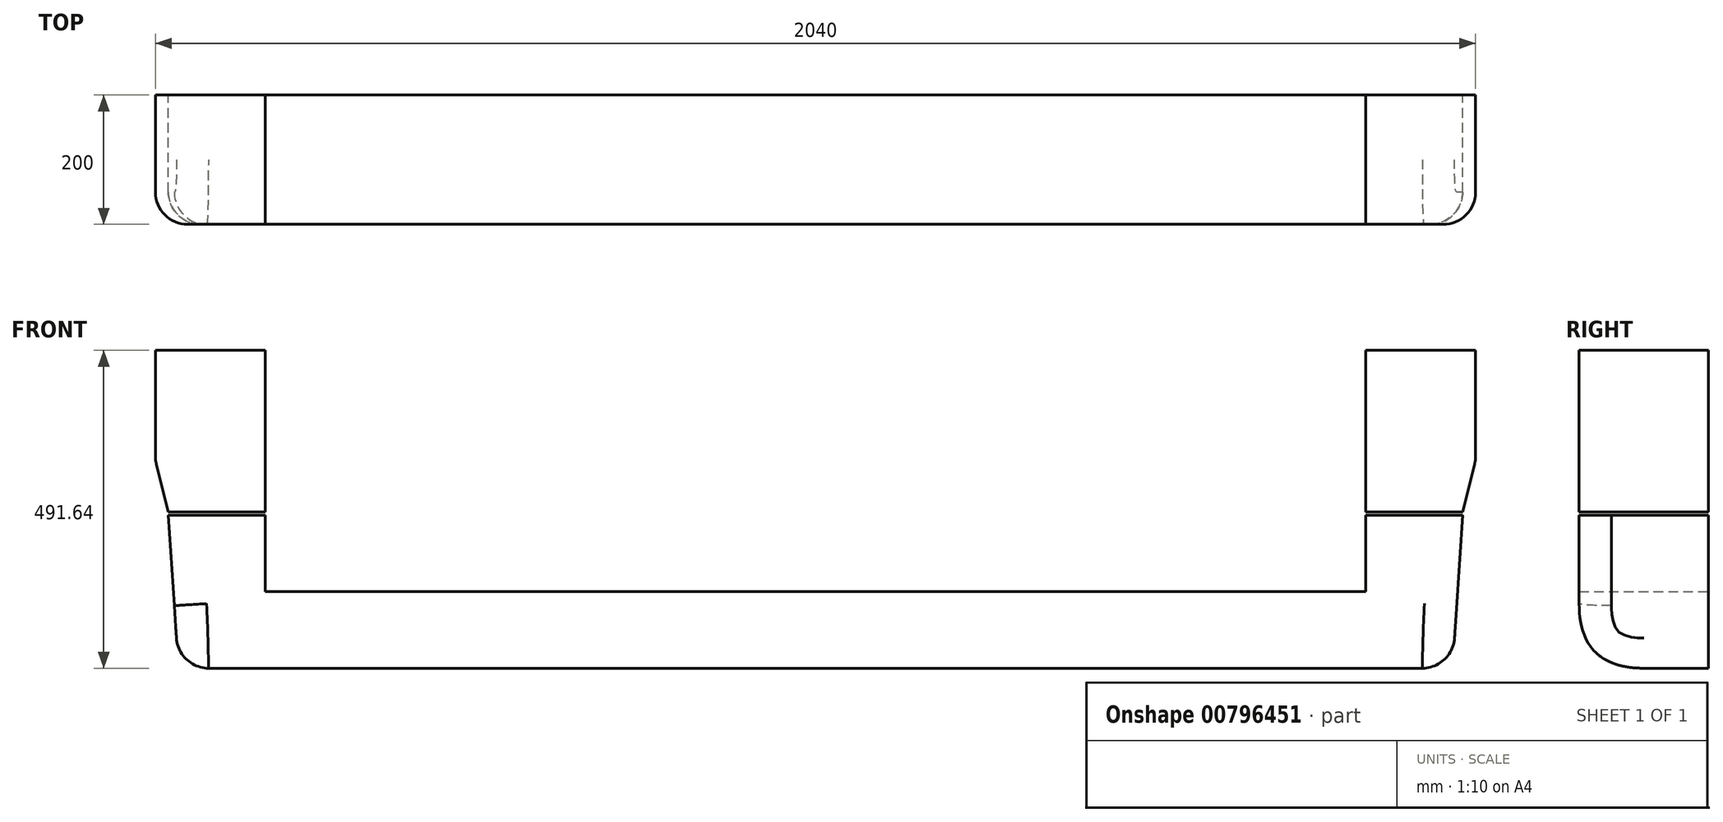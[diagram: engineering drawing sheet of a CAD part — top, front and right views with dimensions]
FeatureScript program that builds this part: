
annotation { "Feature Type Name" : "Feature", "Feature Type Description" : "" }
export const myFeature = defineFeature(function(context is Context, id is Id, definition is map)
    precondition{}
    {
        {
            var Q0;
            Q0=qCreatedBy(makeId("Front.planeOp"),FACE);
            var sketch = newSketch(context, id + "F0", { "sketchPlane" : qUnion([Q0])});
            skLineSegment(sketch, "E0.top", {"start": v(0, -118.32) * mm, "end": v(-950, -118.32) * mm});
            skPoint(sketch, "E0.middle", {"position": v(0, 0) * mm});
            skLineSegment(sketch, "E1.top", {"start": v(-850, 0) * mm, "end": v(0, 0) * mm});
            skLineSegment(sketch, "E1.left", {"start": v(-850, 118.32) * mm, "end": v(-850, 0) * mm});
            skLineSegment(sketch, "E2.trimOffspring", {"start": v(-850, 118.32) * mm, "end": v(-1000, 118.32) * mm});
            skPoint(sketch, "E3.visualSharp", {"position": v(-1000, -118.32) * mm});
            skArc(sketch, "E3.filletArc", {"start": v(-985.36, -103.67) * mm, "mid": v(-969.13, -114.51) * mm, "end": v(-950, -118.32) * mm});
            skPoint(sketch, "E4.visualSharp", {"position": v(1000, -118.32) * mm});
            skLineSegment(sketch, "E5", {"start": v(-1000, 123.32) * mm, "end": v(-850, 123.32) * mm});
            skLineSegment(sketch, "E6", {"start": v(-850, 123.32) * mm, "end": v(-850, 373.32) * mm});
            skLineSegment(sketch, "E7", {"start": v(-850, 373.32) * mm, "end": v(-1000, 373.32) * mm});
            skLineSegment(sketch, "E8", {"start": v(-1000, 118.32) * mm, "end": v(-985.36, -103.67) * mm});
            skLineSegment(sketch, "E9", {"start": v(-1020, 209.43) * mm, "end": v(-1020, 373.32) * mm});
            skLineSegment(sketch, "E10", {"start": v(-1020, 373.32) * mm, "end": v(-1000, 373.32) * mm});
            skLineSegment(sketch, "E11", {"start": v(-1000, 123.32) * mm, "end": v(-1018.5, 197.3) * mm});
            skPoint(sketch, "E12.end.orphan", {"position": v(-1020, 153.28) * mm});
            skPoint(sketch, "E13.visualSharp", {"position": v(-1020, 203.28) * mm});
            skArc(sketch, "E13.filletArc", {"start": v(-1020, 209.43) * mm, "mid": v(-1019.63, 203.32) * mm, "end": v(-1018.5, 197.3) * mm});
            skLineSegment(sketch, "E14", {"start": v(0, 0) * mm, "end": v(0, -118.32) * mm});
            skPoint(sketch, "E1.right.end.orphan", {"position": v(850, 0) * mm});
            skPoint(sketch, "E0.bottom.end.orphan", {"position": v(850, 118.32) * mm});
            skPoint(sketch, "E4.filletArc.start.orphan", {"position": v(950, -118.32) * mm});
            skPoint(sketch, "E15.start.orphan", {"position": v(1000, 118.32) * mm});
            skPoint(sketch, "E16.start.orphan", {"position": v(1000, 123.32) * mm});
            skPoint(sketch, "E17.end.orphan", {"position": v(850, 123.32) * mm});
            skPoint(sketch, "E18.end.orphan", {"position": v(850, 373.32) * mm});
            skLineSegment(sketch, "E19.MirrorCS", {"start": v(850, 0) * mm, "end": v(0, 0) * mm});
            skLineSegment(sketch, "E20.MirrorCS", {"start": v(0, -118.32) * mm, "end": v(950, -118.32) * mm});
            skArc(sketch, "E21.MirrorCS", {"start": v(985.36, -103.67) * mm, "mid": v(969.13, -114.51) * mm, "end": v(950, -118.32) * mm});
            skLineSegment(sketch, "E22.MirrorCS", {"start": v(1000, 118.32) * mm, "end": v(985.36, -103.67) * mm});
            skLineSegment(sketch, "E23.MirrorCS", {"start": v(850, 118.32) * mm, "end": v(850, 0) * mm});
            skLineSegment(sketch, "E24.MirrorCS", {"start": v(850, 123.32) * mm, "end": v(850, 373.32) * mm});
            skLineSegment(sketch, "E25.MirrorCS", {"start": v(1000, 123.32) * mm, "end": v(1018.5, 197.3) * mm});
            skArc(sketch, "E26.MirrorCS", {"start": v(1020, 209.43) * mm, "mid": v(1019.63, 203.32) * mm, "end": v(1018.5, 197.3) * mm});
            skLineSegment(sketch, "E27.MirrorCS", {"start": v(1020, 209.43) * mm, "end": v(1020, 373.32) * mm});
            skLineSegment(sketch, "E28.MirrorCS", {"start": v(1020, 373.32) * mm, "end": v(1000, 373.32) * mm});
            skLineSegment(sketch, "E29.MirrorCS", {"start": v(850, 373.32) * mm, "end": v(1000, 373.32) * mm});
            skLineSegment(sketch, "E30.MirrorCS", {"start": v(1000, 123.32) * mm, "end": v(850, 123.32) * mm});
            skLineSegment(sketch, "E31.MirrorCS", {"start": v(850, 118.32) * mm, "end": v(1000, 118.32) * mm});
            skSolve(sketch);
        }
        {
            var Q0;
            Q0=makeQuery(id+"F0.imprint","IMPRINT",FACE,{"disambiguationData":[TD([[makeQuery(id+"F0.imprint","IMPRINT",EDGE,{"derivedFrom":sQuery(id+"F0.wireOp",EDGE,"E14")}),1.0]])]});
            var Q1;
            Q1=makeQuery(id+"F0.imprint","IMPRINT",FACE,{"disambiguationData":[TD([[makeQuery(id+"F0.imprint","IMPRINT",EDGE,{"derivedFrom":sQuery(id+"F0.wireOp",EDGE,"E0.top")}),-1.0]])]});
            var Q2;
            Q2=makeQuery(id+"F0.imprint","IMPRINT",FACE,{"disambiguationData":[TD([[makeQuery(id+"F0.imprint","IMPRINT",EDGE,{"derivedFrom":sQuery(id+"F0.wireOp",EDGE,"E5")}),1.0]])]});
            var Q3;
            Q3=makeQuery(id+"F0.imprint","IMPRINT",FACE,{"disambiguationData":[TD([[makeQuery(id+"F0.imprint","IMPRINT",EDGE,{"derivedFrom":sQuery(id+"F0.wireOp",EDGE,"E25.MirrorCS")}),1.0]])]});
            extrude(context, id + "F1", {"entities" : qUnion([Q0, Q1, Q2, Q3]), "depth" : 200 * mm, "offsetDistance" : 25.4 * mm});
        }
        {
            var Q0;
            Q0=makeQuery(id+"F1.opExtrude","CAP_EDGE",EDGE,{"disambiguationData":[OSD([sQuery(id+"F0.wireOp",EDGE,"E0.left")])],"isStart":false});
            var Q1;
            Q1=makeQuery(id+"F1.opExtrude","CAP_EDGE",EDGE,{"disambiguationData":[OSD([sQuery(id+"F0.wireOp",EDGE,"E4.filletArc")])],"isStart":false});
            var Q2;
            Q2=makeQuery(id+"F1.opExtrude","CAP_EDGE",EDGE,{"disambiguationData":[OSD([sQuery(id+"F0.wireOp",EDGE,"E0.top")])],"isStart":false});
            var Q3;
            Q3=makeQuery(id+"F1.opExtrude","CAP_EDGE",EDGE,{"disambiguationData":[OSD([sQuery(id+"F0.wireOp",EDGE,"E3.filletArc")])],"isStart":false});
            var Q4;
            Q4=makeQuery(id+"F1.opExtrude","CAP_EDGE",EDGE,{"disambiguationData":[OSD([sQuery(id+"F0.wireOp",EDGE,"E0.right")])],"isStart":false});
            fillet(context, id + "F2", {"entities" : qUnion([Q0, Q1, Q2, Q3, Q4]), "radius" : 100 * mm, "tangentPropagation" : true, "rho" : 0.5, "crossSection" : FilletCrossSection.CONIC, "allowEdgeOverflow" : false});
        }
        {
            var Q0;
            Q0=makeQuery(id+"F2.opFillet","BLEND_EDGE",EDGE,{"blendedFrom":[makeQuery(id+"F1.opExtrude","CAP_EDGE",EDGE,{"disambiguationData":[OSD([sQuery(id+"F0.wireOp",EDGE,"E0.top"),sQuery(id+"F0.wireOp",EDGE,"E20.MirrorCS")])],"isStart":false}),makeQuery(id+"F1.opExtrude","SWEPT_FACE",FACE,{"disambiguationData":[OSD([sQuery(id+"F0.wireOp",EDGE,"E8")])]})],"blendedInto":[makeQuery(id+"F1.opExtrude","SWEPT_FACE",FACE,{"disambiguationData":[OSD([sQuery(id+"F0.wireOp",EDGE,"E8")])]})]});
            var Q1;
            Q1=makeQuery(id+"F1.opExtrude","CAP_EDGE",EDGE,{"disambiguationData":[OSD([sQuery(id+"F0.wireOp",EDGE,"E8")])],"isStart":false});
            var Q2;
            Q2=makeQuery(id+"F1.opExtrude","CAP_EDGE",EDGE,{"disambiguationData":[OSD([sQuery(id+"F0.wireOp",EDGE,"E11")])],"isStart":false});
            var Q3;
            Q3=makeQuery(id+"F1.opExtrude","CAP_EDGE",EDGE,{"disambiguationData":[OSD([sQuery(id+"F0.wireOp",EDGE,"E13.filletArc")])],"isStart":false});
            var Q4;
            Q4=makeQuery(id+"F1.opExtrude","CAP_EDGE",EDGE,{"disambiguationData":[OSD([sQuery(id+"F0.wireOp",EDGE,"E9")])],"isStart":false});
            var Q5;
            Q5=makeQuery(id+"F2.opFillet","BLEND_EDGE",EDGE,{"blendedFrom":[makeQuery(id+"F1.opExtrude","CAP_EDGE",EDGE,{"disambiguationData":[OSD([sQuery(id+"F0.wireOp",EDGE,"E0.top"),sQuery(id+"F0.wireOp",EDGE,"E20.MirrorCS")])],"isStart":false}),makeQuery(id+"F1.opExtrude","SWEPT_FACE",FACE,{"disambiguationData":[OSD([sQuery(id+"F0.wireOp",EDGE,"E22.MirrorCS")])]})],"blendedInto":[makeQuery(id+"F1.opExtrude","SWEPT_FACE",FACE,{"disambiguationData":[OSD([sQuery(id+"F0.wireOp",EDGE,"E22.MirrorCS")])]})]});
            var Q6;
            Q6=makeQuery(id+"F1.opExtrude","CAP_EDGE",EDGE,{"disambiguationData":[OSD([sQuery(id+"F0.wireOp",EDGE,"E25.MirrorCS")])],"isStart":false});
            var Q7;
            Q7=makeQuery(id+"F1.opExtrude","CAP_EDGE",EDGE,{"disambiguationData":[OSD([sQuery(id+"F0.wireOp",EDGE,"E27.MirrorCS")])],"isStart":false});
            var Q8;
            Q8=makeQuery(id+"F1.opExtrude","CAP_EDGE",EDGE,{"disambiguationData":[OSD([sQuery(id+"F0.wireOp",EDGE,"E26.MirrorCS")])],"isStart":false});
            fillet(context, id + "F3", {"entities" : qUnion([Q0, Q1, Q2, Q3, Q4, Q5, Q6, Q7, Q8]), "radius" : 50 * mm, "allowEdgeOverflow" : false});
        }
    });
